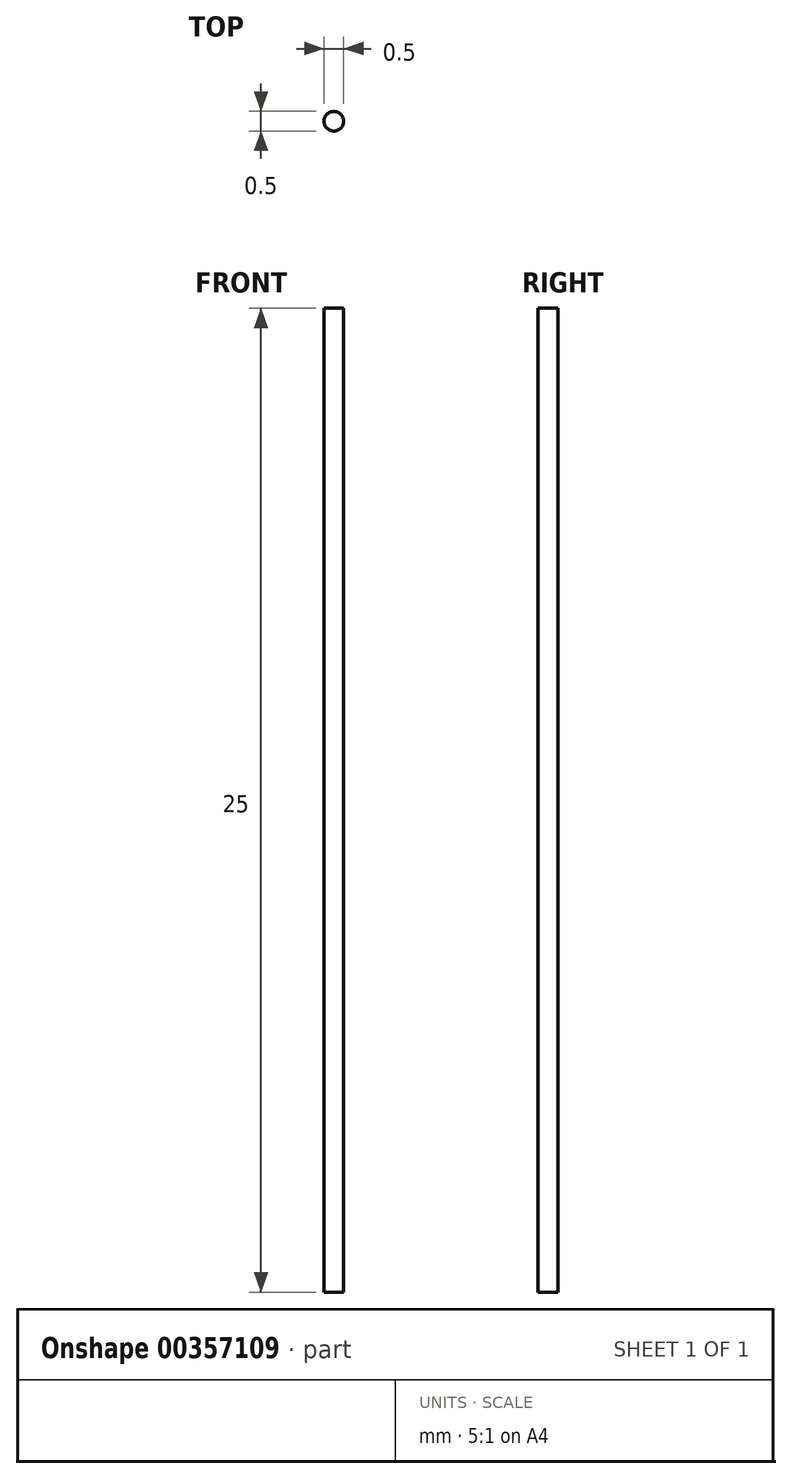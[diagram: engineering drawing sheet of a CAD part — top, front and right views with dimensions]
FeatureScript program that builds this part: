
annotation { "Feature Type Name" : "Feature", "Feature Type Description" : "" }
export const myFeature = defineFeature(function(context is Context, id is Id, definition is map)
    precondition{}
    {
        {
            var Q0;
            Q0=qCreatedBy(makeId("Top.planeOp"),FACE);
            var sketch = newSketch(context, id + "F0", { "sketchPlane" : qUnion([Q0])});
            skCircle(sketch, "E0", {"center": v(0, 0) * mm, "radius": 0.25 * mm});
            skSolve(sketch);
        }
        {
            var Q0;
            Q0 = qSketchRegion(id + "F0", true);
            extrude(context, id + "F1", {"entities" : qUnion([Q0]), "depth" : 25 * mm});
        }
    });
